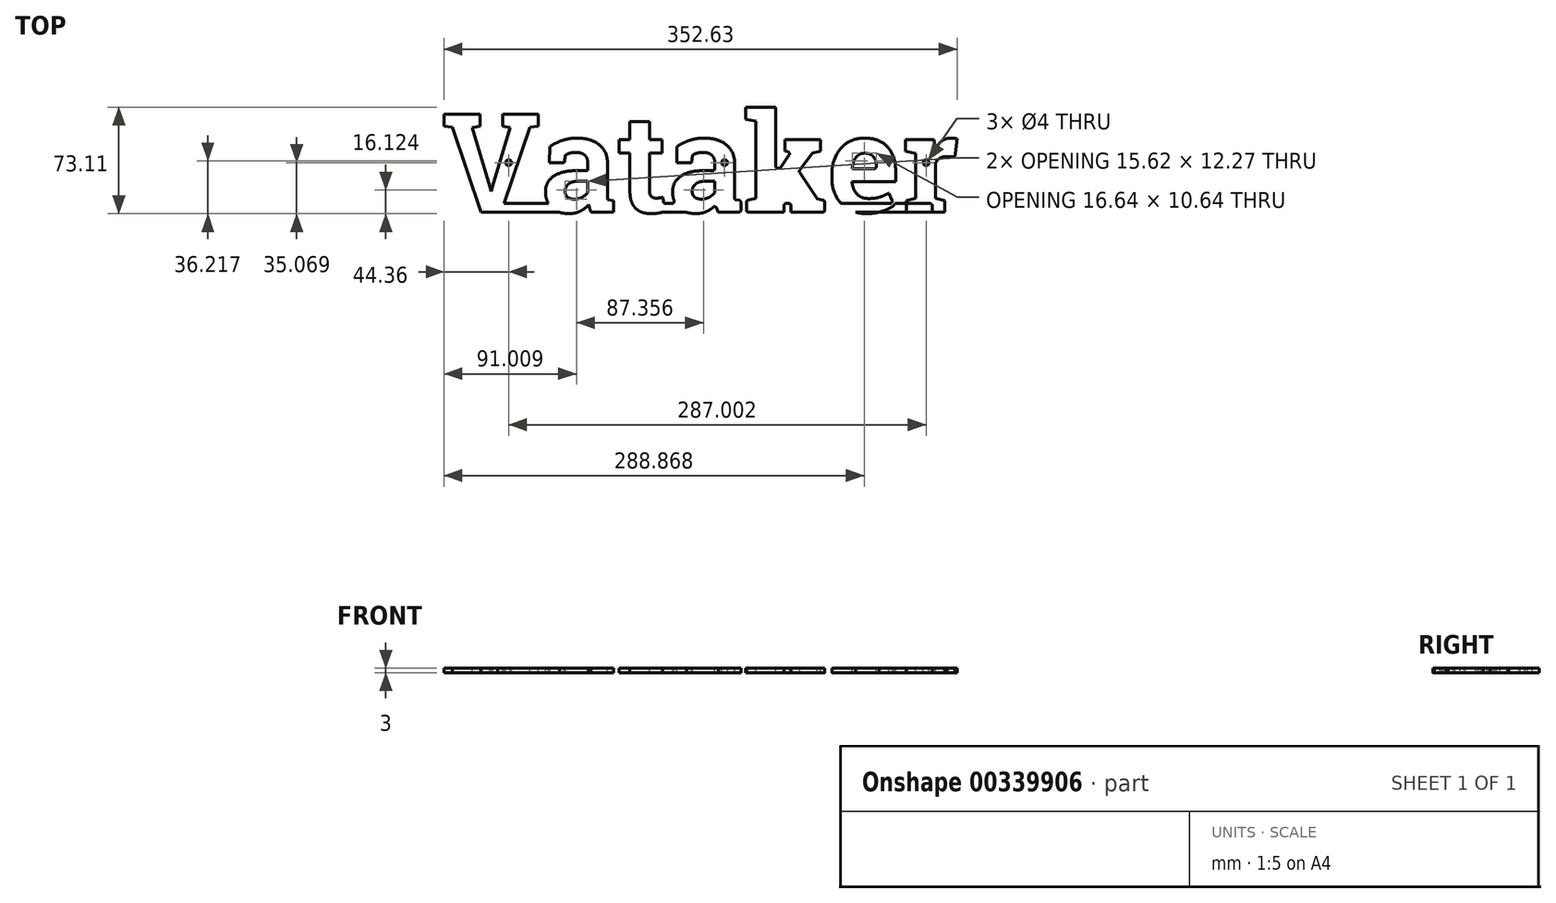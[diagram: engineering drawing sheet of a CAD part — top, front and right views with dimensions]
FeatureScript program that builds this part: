
annotation { "Feature Type Name" : "Feature", "Feature Type Description" : "" }
export const myFeature = defineFeature(function(context is Context, id is Id, definition is map)
    precondition{}
    {
        {
            var Q0;
            Q0=qCreatedBy(makeId("Top.planeOp"),FACE);
            var sketch = newSketch(context, id + "F0", { "sketchPlane" : qUnion([Q0])});
            skLineSegment(sketch, "E0.left", {"start": v(-86.93, -62.9) * mm, "end": v(-86.93, -77.95) * mm});
            skText(sketch, "E1", { "text": "Vataker ", "fontName": "RobotoSlab-Bold.ttf"});
            skLineSegment(sketch, "E2.bottom", {"start": v(-195.52, 95.97) * mm, "end": v(103.03, 95.97) * mm});
            skLineSegment(sketch, "E2.top", {"start": v(-195.52, 89.97) * mm, "end": v(103.03, 89.97) * mm});
            skLineSegment(sketch, "E2.left", {"start": v(-195.52, 95.97) * mm, "end": v(-195.52, 89.97) * mm});
            skLineSegment(sketch, "E2.right", {"start": v(103.03, 95.97) * mm, "end": v(103.03, 89.97) * mm});
            skLineSegment(sketch, "E3", {"start": v(-234.05, 124.06) * mm, "end": v(125.95, 124.06) * mm, "construction": true});
            skCircle(sketch, "E4", {"center": v(-188.12, 124.06) * mm, "radius": 2 * mm});
            skCircle(sketch, "E5", {"center": v(-39.65, 124.06) * mm, "radius": 2 * mm});
            skCircle(sketch, "E6", {"center": v(98.88, 124.06) * mm, "radius": 2 * mm});
            const initialGuessF0  = {"E1": [-0.23405, 0.08997, 1, 0, 0.06818]};
            skSetInitialGuess(sketch, initialGuessF0);
            skSolve(sketch);
        }
        {
            var Q0;
            Q0=makeQuery(id+"F0.imprint","IMPRINT",FACE,{"disambiguationData":[TD([[makeQuery(id+"F0.imprint","IMPRINT",EDGE,{"derivedFrom":sQuery(id+"F0.wireOp",EDGE,"E1.sketch_text.stroke-0")}),-1.0]])]});
            var Q1;
            {var subQ0=sQuery(id+"F0.wireOp",EDGE,"E1.sketch_text.stroke-22");var subQ1=sQuery(id+"F0.wireOp",EDGE,"E1.sketch_text.stroke-21");var subQ2=makeQuery(id+"F0.imprint","INTERSECT",VERTEX,{"derivedFrom":[subQ1,subQ0]});Q1=makeQuery(id+"F0.imprint","IMPRINT",FACE,{"disambiguationData":[TD([[makeQuery(id+"F0.imprint","IMPRINT",EDGE,{"disambiguationData":[TD([[subQ2,1.0]])],"derivedFrom":subQ1}),-1.0]])]});}
            var Q2;
            Q2=makeQuery(id+"F0.imprint","IMPRINT",FACE,{"disambiguationData":[TD([[makeQuery(id+"F0.imprint","IMPRINT",EDGE,{"derivedFrom":sQuery(id+"F0.wireOp",EDGE,"E1.sketch_text.stroke-53")}),-1.0]])]});
            var Q3;
            {var subQ0=sQuery(id+"F0.wireOp",EDGE,"E1.sketch_text.stroke-64");Q3=makeQuery(id+"F0.imprint","IMPRINT",FACE,{"disambiguationData":[TD([[makeQuery(id+"F0.imprint","IMPRINT",EDGE,{"derivedFrom":subQ0}),-1.0]])]});}
            var Q4;
            {var subQ0=sQuery(id+"F0.wireOp",EDGE,"E1.sketch_text.stroke-77");var subQ1=sQuery(id+"F0.wireOp",EDGE,"E1.sketch_text.stroke-76");var subQ2=makeQuery(id+"F0.imprint","INTERSECT",VERTEX,{"derivedFrom":[subQ1,subQ0]});Q4=makeQuery(id+"F0.imprint","IMPRINT",FACE,{"disambiguationData":[TD([[makeQuery(id+"F0.imprint","IMPRINT",EDGE,{"disambiguationData":[TD([[subQ2,1.0]])],"derivedFrom":subQ1}),-1.0]])]});}
            var Q5;
            {var subQ0=sQuery(id+"F0.wireOp",EDGE,"E1.sketch_text.stroke-151");var subQ1=sQuery(id+"F0.wireOp",EDGE,"E1.sketch_text.stroke-135");var subQ2=makeQuery(id+"F0.imprint","INTERSECT",VERTEX,{"derivedFrom":[subQ1,subQ0]});Q5=makeQuery(id+"F0.imprint","IMPRINT",FACE,{"disambiguationData":[TD([[makeQuery(id+"F0.imprint","IMPRINT",EDGE,{"disambiguationData":[TD([[subQ2,-1.0]])],"derivedFrom":subQ1}),-1.0]])]});}
            var Q6;
            {var subQ0=sQuery(id+"F0.wireOp",EDGE,"E1.sketch_text.stroke-159");Q6=makeQuery(id+"F0.imprint","IMPRINT",FACE,{"disambiguationData":[TD([[makeQuery(id+"F0.imprint","IMPRINT",EDGE,{"derivedFrom":subQ0}),-1.0]])]});}
            var Q7;
            {var subQ5=sQuery(id+"F0.wireOp",EDGE,"E2.right");Q7=makeQuery(id+"F0.imprint","IMPRINT",FACE,{"disambiguationData":[TD([[makeQuery(id+"F0.imprint","IMPRINT",EDGE,{"derivedFrom":subQ5}),-1.0]])]});}
            var Q8;
            {var subQ5=sQuery(id+"F0.wireOp",EDGE,"E2.top");var subQ6=sQuery(id+"F0.wireOp",EDGE,"E1.sketch_text.stroke-11");var subQ7=makeQuery(id+"F0.imprint","INTERSECT",VERTEX,{"derivedFrom":[subQ6,subQ5]});Q8=makeQuery(id+"F0.imprint","IMPRINT",FACE,{"disambiguationData":[TD([[makeQuery(id+"F0.imprint","IMPRINT",EDGE,{"disambiguationData":[TD([[subQ7,1.0]])],"derivedFrom":subQ6}),1.0]])]});}
            var Q9;
            {var subQ5=sQuery(id+"F0.wireOp",EDGE,"E2.left");Q9=makeQuery(id+"F0.imprint","IMPRINT",FACE,{"disambiguationData":[TD([[makeQuery(id+"F0.imprint","IMPRINT",EDGE,{"derivedFrom":subQ5}),1.0]])]});}
            var Q10;
            {var subQ4=sQuery(id+"F0.wireOp",EDGE,"E1.sketch_text.stroke-24");Q10=makeQuery(id+"F0.imprint","IMPRINT",FACE,{"disambiguationData":[TD([[makeQuery(id+"F0.imprint","IMPRINT",EDGE,{"derivedFrom":subQ4}),-1.0]])]});}
            var Q11;
            {var subQ1=sQuery(id+"F0.wireOp",EDGE,"E1.sketch_text.stroke-43");var subQ7=sQuery(id+"F0.wireOp",EDGE,"E2.top");var subQ9=makeQuery(id+"F0.imprint","INTERSECT",VERTEX,{"derivedFrom":[subQ1,subQ7]});Q11=makeQuery(id+"F0.imprint","IMPRINT",FACE,{"disambiguationData":[TD([[makeQuery(id+"F0.imprint","IMPRINT",EDGE,{"disambiguationData":[TD([[subQ9,1.0]])],"derivedFrom":subQ1}),1.0]])]});}
            var Q12;
            {var subQ5=sQuery(id+"F0.wireOp",EDGE,"E1.sketch_text.stroke-63");var subQ6=sQuery(id+"F0.wireOp",EDGE,"E1.sketch_text.stroke-62");var subQ7=makeQuery(id+"F0.imprint","INTERSECT",VERTEX,{"derivedFrom":[subQ6,subQ5]});Q12=makeQuery(id+"F0.imprint","IMPRINT",FACE,{"disambiguationData":[TD([[makeQuery(id+"F0.imprint","IMPRINT",EDGE,{"disambiguationData":[TD([[subQ7,1.0]])],"derivedFrom":subQ6}),1.0]])]});}
            var Q13;
            {var subQ6=sQuery(id+"F0.wireOp",EDGE,"E1.sketch_text.stroke-79");Q13=makeQuery(id+"F0.imprint","IMPRINT",FACE,{"disambiguationData":[TD([[makeQuery(id+"F0.imprint","IMPRINT",EDGE,{"derivedFrom":subQ6}),-1.0]])]});}
            var Q14;
            {var subQ0=sQuery(id+"F0.wireOp",EDGE,"E2.top");var subQ1=sQuery(id+"F0.wireOp",EDGE,"E1.sketch_text.stroke-98");var subQ2=makeQuery(id+"F0.imprint","INTERSECT",VERTEX,{"derivedFrom":[subQ1,subQ0]});Q14=makeQuery(id+"F0.imprint","IMPRINT",FACE,{"disambiguationData":[TD([[makeQuery(id+"F0.imprint","IMPRINT",EDGE,{"disambiguationData":[TD([[subQ2,1.0]])],"derivedFrom":subQ1}),1.0]])]});}
            var Q15;
            {var subQ1=sQuery(id+"F0.wireOp",EDGE,"E1.sketch_text.stroke-121");var subQ7=sQuery(id+"F0.wireOp",EDGE,"E2.top");var subQ8=makeQuery(id+"F0.imprint","INTERSECT",VERTEX,{"derivedFrom":[subQ1,subQ7]});Q15=makeQuery(id+"F0.imprint","IMPRINT",FACE,{"disambiguationData":[TD([[makeQuery(id+"F0.imprint","IMPRINT",EDGE,{"disambiguationData":[TD([[subQ8,1.0]])],"derivedFrom":subQ1}),1.0]])]});}
            var Q16;
            {var subQ0=sQuery(id+"F0.wireOp",EDGE,"E1.sketch_text.stroke-137");Q16=makeQuery(id+"F0.imprint","IMPRINT",FACE,{"disambiguationData":[TD([[makeQuery(id+"F0.imprint","IMPRINT",EDGE,{"derivedFrom":subQ0}),-1.0]])]});}
            var Q17;
            {var subQ6=sQuery(id+"F0.wireOp",EDGE,"E1.sketch_text.stroke-150");Q17=makeQuery(id+"F0.imprint","IMPRINT",FACE,{"disambiguationData":[TD([[makeQuery(id+"F0.imprint","IMPRINT",EDGE,{"derivedFrom":subQ6}),1.0]])]});}
            var Q18;
            Q18=makeQuery(id+"F0.imprint","IMPRINT",FACE,{"disambiguationData":[TD([[makeQuery(id+"F0.imprint","IMPRINT",EDGE,{"derivedFrom":sQuery(id+"F0.wireOp",EDGE,"E1.sketch_text.stroke-108")}),-1.0]])]});
            var Q19;
            {var subQ0=sQuery(id+"F0.wireOp",EDGE,"E2.top");var subQ1=sQuery(id+"F0.wireOp",EDGE,"E1.sketch_text.stroke-121");var subQ2=makeQuery(id+"F0.imprint","INTERSECT",VERTEX,{"derivedFrom":[subQ1,subQ0]});Q19=makeQuery(id+"F0.imprint","IMPRINT",FACE,{"disambiguationData":[TD([[makeQuery(id+"F0.imprint","IMPRINT",EDGE,{"disambiguationData":[TD([[subQ2,1.0]])],"derivedFrom":subQ1}),-1.0]])]});}
            var Q20;
            {var subQ0=sQuery(id+"F0.wireOp",EDGE,"E2.top");var subQ1=sQuery(id+"F0.wireOp",EDGE,"E1.sketch_text.stroke-123");var subQ2=makeQuery(id+"F0.imprint","INTERSECT",VERTEX,{"derivedFrom":[subQ1,subQ0]});Q20=makeQuery(id+"F0.imprint","IMPRINT",FACE,{"disambiguationData":[TD([[makeQuery(id+"F0.imprint","IMPRINT",EDGE,{"disambiguationData":[TD([[subQ2,-1.0]])],"derivedFrom":subQ1}),1.0]])]});}
            var Q21;
            {var subQ0=sQuery(id+"F0.wireOp",EDGE,"E2.top");var subQ1=sQuery(id+"F0.wireOp",EDGE,"E1.sketch_text.stroke-129");var subQ2=makeQuery(id+"F0.imprint","INTERSECT",VERTEX,{"derivedFrom":[subQ1,subQ0]});Q21=makeQuery(id+"F0.imprint","IMPRINT",FACE,{"disambiguationData":[TD([[makeQuery(id+"F0.imprint","IMPRINT",EDGE,{"disambiguationData":[TD([[subQ2,1.0]])],"derivedFrom":subQ1}),-1.0]])]});}
            var Q22;
            {var subQ0=sQuery(id+"F0.wireOp",EDGE,"E2.top");var subQ1=sQuery(id+"F0.wireOp",EDGE,"E1.sketch_text.stroke-175");var subQ2=makeQuery(id+"F0.imprint","INTERSECT",VERTEX,{"derivedFrom":[subQ1,subQ0]});Q22=makeQuery(id+"F0.imprint","IMPRINT",FACE,{"disambiguationData":[TD([[makeQuery(id+"F0.imprint","IMPRINT",EDGE,{"disambiguationData":[TD([[subQ2,1.0]])],"derivedFrom":subQ1}),-1.0]])]});}
            var Q23;
            {var subQ5=sQuery(id+"F0.wireOp",EDGE,"E1.sketch_text.stroke-63");var subQ6=sQuery(id+"F0.wireOp",EDGE,"E1.sketch_text.stroke-62");var subQ7=makeQuery(id+"F0.imprint","INTERSECT",VERTEX,{"derivedFrom":[subQ6,subQ5]});Q23=makeQuery(id+"F0.imprint","IMPRINT",FACE,{"disambiguationData":[TD([[makeQuery(id+"F0.imprint","IMPRINT",EDGE,{"disambiguationData":[TD([[subQ7,1.0]])],"derivedFrom":subQ6}),-1.0]])]});}
            var Q24;
            {var subQ0=sQuery(id+"F0.wireOp",EDGE,"E1.sketch_text.stroke-150");Q24=makeQuery(id+"F0.imprint","IMPRINT",FACE,{"disambiguationData":[TD([[makeQuery(id+"F0.imprint","IMPRINT",EDGE,{"derivedFrom":subQ0}),-1.0]])]});}
            var Q25;
            {var subQ9=sQuery(id+"F0.wireOp",EDGE,"E1.sketch_text.stroke-18");Q25=makeQuery(id+"F0.imprint","IMPRINT",FACE,{"disambiguationData":[TD([[makeQuery(id+"F0.imprint","IMPRINT",EDGE,{"derivedFrom":subQ9}),-1.0]])]});}
            var Q26;
            {var subQ4=sQuery(id+"F0.wireOp",EDGE,"E1.sketch_text.stroke-73");Q26=makeQuery(id+"F0.imprint","IMPRINT",FACE,{"disambiguationData":[TD([[makeQuery(id+"F0.imprint","IMPRINT",EDGE,{"derivedFrom":subQ4}),-1.0]])]});}
            var Q27;
            {var subQ5=sQuery(id+"F0.wireOp",EDGE,"E1.sketch_text.stroke-21");var subQ6=sQuery(id+"F0.wireOp",EDGE,"E1.sketch_text.stroke-20");var subQ7=makeQuery(id+"F0.imprint","INTERSECT",VERTEX,{"derivedFrom":[subQ6,subQ5]});Q27=makeQuery(id+"F0.imprint","IMPRINT",FACE,{"disambiguationData":[TD([[makeQuery(id+"F0.imprint","IMPRINT",EDGE,{"disambiguationData":[TD([[subQ7,1.0]])],"derivedFrom":subQ6}),-1.0]])]});}
            var Q28;
            {var subQ5=sQuery(id+"F0.wireOp",EDGE,"E1.sketch_text.stroke-76");var subQ6=sQuery(id+"F0.wireOp",EDGE,"E1.sketch_text.stroke-75");var subQ7=makeQuery(id+"F0.imprint","INTERSECT",VERTEX,{"derivedFrom":[subQ6,subQ5]});Q28=makeQuery(id+"F0.imprint","IMPRINT",FACE,{"disambiguationData":[TD([[makeQuery(id+"F0.imprint","IMPRINT",EDGE,{"disambiguationData":[TD([[subQ7,1.0]])],"derivedFrom":subQ6}),-1.0]])]});}
            extrude(context, id + "F1", {"entities" : qUnion([Q0, Q1, Q2, Q3, Q4, Q5, Q6, Q7, Q8, Q9, Q10, Q11, Q12, Q13, Q14, Q15, Q16, Q17, Q18, Q19, Q20, Q21, Q22, Q23, Q24, Q25, Q26, Q27, Q28]), "oppositeDirection" : true, "depth" : 3 * mm, "offsetDistance" : 25 * mm});
        }
        {
            var Q0;
            Q0=makeQuery(id+"F1.opExtrude","SWEPT_EDGE",EDGE,{"disambiguationData":[OSD([sQuery(id+"F0.wireOp",EDGE,"E1.sketch_text.stroke-11"),sQuery(id+"F0.wireOp",EDGE,"E2.bottom")])]});
            var Q1;
            Q1=makeQuery(id+"F1.opExtrude","SWEPT_EDGE",EDGE,{"disambiguationData":[OSD([sQuery(id+"F0.wireOp",EDGE,"E1.sketch_text.stroke-43"),sQuery(id+"F0.wireOp",EDGE,"E2.bottom")])]});
            var Q2;
            Q2=makeQuery(id+"F1.opExtrude","SWEPT_EDGE",EDGE,{"disambiguationData":[OSD([sQuery(id+"F0.wireOp",EDGE,"E1.sketch_text.stroke-62"),sQuery(id+"F0.wireOp",EDGE,"E2.bottom")])]});
            var Q3;
            Q3=makeQuery(id+"F1.opExtrude","SWEPT_EDGE",EDGE,{"disambiguationData":[OSD([sQuery(id+"F0.wireOp",EDGE,"E1.sketch_text.stroke-78"),sQuery(id+"F0.wireOp",EDGE,"E2.bottom")])]});
            var Q4;
            Q4=makeQuery(id+"F1.opExtrude","SWEPT_EDGE",EDGE,{"disambiguationData":[OSD([sQuery(id+"F0.wireOp",EDGE,"E1.sketch_text.stroke-66"),sQuery(id+"F0.wireOp",EDGE,"E2.bottom")])]});
            var Q5;
            Q5=makeQuery(id+"F1.opExtrude","SWEPT_EDGE",EDGE,{"disambiguationData":[OSD([sQuery(id+"F0.wireOp",EDGE,"E1.sketch_text.stroke-98"),sQuery(id+"F0.wireOp",EDGE,"E2.bottom")])]});
            var Q6;
            Q6=makeQuery(id+"F1.opExtrude","SWEPT_EDGE",EDGE,{"disambiguationData":[OSD([sQuery(id+"F0.wireOp",EDGE,"E1.sketch_text.stroke-131"),sQuery(id+"F0.wireOp",EDGE,"E2.bottom")])]});
            var Q7;
            Q7=makeQuery(id+"F1.opExtrude","SWEPT_EDGE",EDGE,{"disambiguationData":[OSD([sQuery(id+"F0.wireOp",EDGE,"E1.sketch_text.stroke-129"),sQuery(id+"F0.wireOp",EDGE,"E2.bottom")])]});
            var Q8;
            Q8=makeQuery(id+"F1.opExtrude","SWEPT_EDGE",EDGE,{"disambiguationData":[OSD([sQuery(id+"F0.wireOp",EDGE,"E1.sketch_text.stroke-123"),sQuery(id+"F0.wireOp",EDGE,"E2.bottom")])]});
            var Q9;
            Q9=makeQuery(id+"F1.opExtrude","SWEPT_EDGE",EDGE,{"disambiguationData":[OSD([sQuery(id+"F0.wireOp",EDGE,"E1.sketch_text.stroke-121"),sQuery(id+"F0.wireOp",EDGE,"E2.bottom")])]});
            var Q10;
            Q10=makeQuery(id+"F1.opExtrude","SWEPT_EDGE",EDGE,{"disambiguationData":[OSD([sQuery(id+"F0.wireOp",EDGE,"E1.sketch_text.stroke-136"),sQuery(id+"F0.wireOp",EDGE,"E2.bottom")])]});
            var Q11;
            Q11=makeQuery(id+"F1.opExtrude","SWEPT_EDGE",EDGE,{"disambiguationData":[OSD([sQuery(id+"F0.wireOp",EDGE,"E1.sketch_text.stroke-149"),sQuery(id+"F0.wireOp",EDGE,"E2.bottom")])]});
            var Q12;
            Q12=makeQuery(id+"F1.opExtrude","SWEPT_EDGE",EDGE,{"disambiguationData":[OSD([sQuery(id+"F0.wireOp",EDGE,"E1.sketch_text.stroke-177"),sQuery(id+"F0.wireOp",EDGE,"E2.bottom")])]});
            var Q13;
            Q13=makeQuery(id+"F1.opExtrude","SWEPT_EDGE",EDGE,{"disambiguationData":[OSD([sQuery(id+"F0.wireOp",EDGE,"E1.sketch_text.stroke-19"),sQuery(id+"F0.wireOp",EDGE,"E1.sketch_text.stroke-20")])]});
            var Q14;
            Q14=makeQuery(id+"F1.opExtrude","SWEPT_EDGE",EDGE,{"disambiguationData":[OSD([sQuery(id+"F0.wireOp",EDGE,"E1.sketch_text.stroke-74"),sQuery(id+"F0.wireOp",EDGE,"E1.sketch_text.stroke-75")])]});
            var Q15;
            Q15=makeQuery(id+"F1.opExtrude","SWEPT_EDGE",EDGE,{"disambiguationData":[OSD([sQuery(id+"F0.wireOp",EDGE,"E1.sketch_text.stroke-153"),sQuery(id+"F0.wireOp",EDGE,"E1.sketch_text.stroke-154")])]});
            var Q16;
            Q16=makeQuery(id+"F1.opExtrude","SWEPT_EDGE",EDGE,{"disambiguationData":[OSD([sQuery(id+"F0.wireOp",EDGE,"E1.sketch_text.stroke-155"),sQuery(id+"F0.wireOp",EDGE,"E1.sketch_text.stroke-156")])]});
            var Q17;
            Q17=makeQuery(id+"F1.opExtrude","SWEPT_EDGE",EDGE,{"disambiguationData":[OSD([sQuery(id+"F0.wireOp",EDGE,"E1.sketch_text.stroke-2"),sQuery(id+"F0.wireOp",EDGE,"E1.sketch_text.stroke-3")])]});
            var Q18;
            Q18=makeQuery(id+"F1.opExtrude","SWEPT_EDGE",EDGE,{"disambiguationData":[OSD([sQuery(id+"F0.wireOp",EDGE,"E1.sketch_text.stroke-3"),sQuery(id+"F0.wireOp",EDGE,"E1.sketch_text.stroke-4")])]});
            var Q19;
            Q19=makeQuery(id+"F1.opExtrude","SWEPT_EDGE",EDGE,{"disambiguationData":[OSD([sQuery(id+"F0.wireOp",EDGE,"E1.sketch_text.stroke-117"),sQuery(id+"F0.wireOp",EDGE,"E1.sketch_text.stroke-118")])]});
            var Q20;
            Q20=makeQuery(id+"F1.opExtrude","SWEPT_EDGE",EDGE,{"disambiguationData":[OSD([sQuery(id+"F0.wireOp",EDGE,"E1.sketch_text.stroke-112"),sQuery(id+"F0.wireOp",EDGE,"E1.sketch_text.stroke-113")])]});
            var Q21;
            Q21=makeQuery(id+"F1.opExtrude","SWEPT_EDGE",EDGE,{"disambiguationData":[OSD([sQuery(id+"F0.wireOp",EDGE,"E1.sketch_text.stroke-125"),sQuery(id+"F0.wireOp",EDGE,"E1.sketch_text.stroke-126")])]});
            var Q22;
            Q22=makeQuery(id+"F1.opExtrude","SWEPT_EDGE",EDGE,{"disambiguationData":[OSD([sQuery(id+"F0.wireOp",EDGE,"E1.sketch_text.stroke-118"),sQuery(id+"F0.wireOp",EDGE,"E1.sketch_text.stroke-119")])]});
            var Q23;
            Q23=makeQuery(id+"F1.opExtrude","SWEPT_EDGE",EDGE,{"disambiguationData":[OSD([sQuery(id+"F0.wireOp",EDGE,"E1.sketch_text.stroke-111"),sQuery(id+"F0.wireOp",EDGE,"E1.sketch_text.stroke-112")])]});
            var Q24;
            Q24=makeQuery(id+"F1.opExtrude","SWEPT_EDGE",EDGE,{"disambiguationData":[OSD([sQuery(id+"F0.wireOp",EDGE,"E1.sketch_text.stroke-126"),sQuery(id+"F0.wireOp",EDGE,"E1.sketch_text.stroke-127")])]});
            var Q25;
            Q25=makeQuery(id+"F1.opExtrude","SWEPT_EDGE",EDGE,{"disambiguationData":[OSD([sQuery(id+"F0.wireOp",EDGE,"E1.sketch_text.stroke-110"),sQuery(id+"F0.wireOp",EDGE,"E1.sketch_text.stroke-111")])]});
            var Q26;
            Q26=makeQuery(id+"F1.opExtrude","SWEPT_EDGE",EDGE,{"disambiguationData":[OSD([sQuery(id+"F0.wireOp",EDGE,"E1.sketch_text.stroke-26"),sQuery(id+"F0.wireOp",EDGE,"E1.sketch_text.stroke-27")])]});
            var Q27;
            Q27=makeQuery(id+"F1.opExtrude","SWEPT_EDGE",EDGE,{"disambiguationData":[OSD([sQuery(id+"F0.wireOp",EDGE,"E1.sketch_text.stroke-81"),sQuery(id+"F0.wireOp",EDGE,"E1.sketch_text.stroke-82")])]});
            fillet(context, id + "F2", {"entities" : qUnion([Q0, Q1, Q2, Q3, Q4, Q5, Q6, Q7, Q8, Q9, Q10, Q11, Q12, Q13, Q14, Q15, Q16, Q17, Q18, Q19, Q20, Q21, Q22, Q23, Q24, Q25, Q26, Q27]), "radius" : 1.5 * mm, "tangentPropagation" : true, "allowEdgeOverflow" : false});
        }
        {
            var Q0;
            Q0=sQuery(id+"F0.wireOp",EDGE,"E4");
            var Q1;
            Q1=sQuery(id+"F0.wireOp",EDGE,"E5");
            var Q2;
            Q2=sQuery(id+"F0.wireOp",EDGE,"E6");
            extrude(context, id + "F3", {"bodyType" : ExtendedToolBodyType.SURFACE, "surfaceEntities" : qUnion([Q0, Q1, Q2]), "oppositeDirection" : true, "depth" : 3 * mm, "offsetDistance" : 25 * mm});
        }
    });
